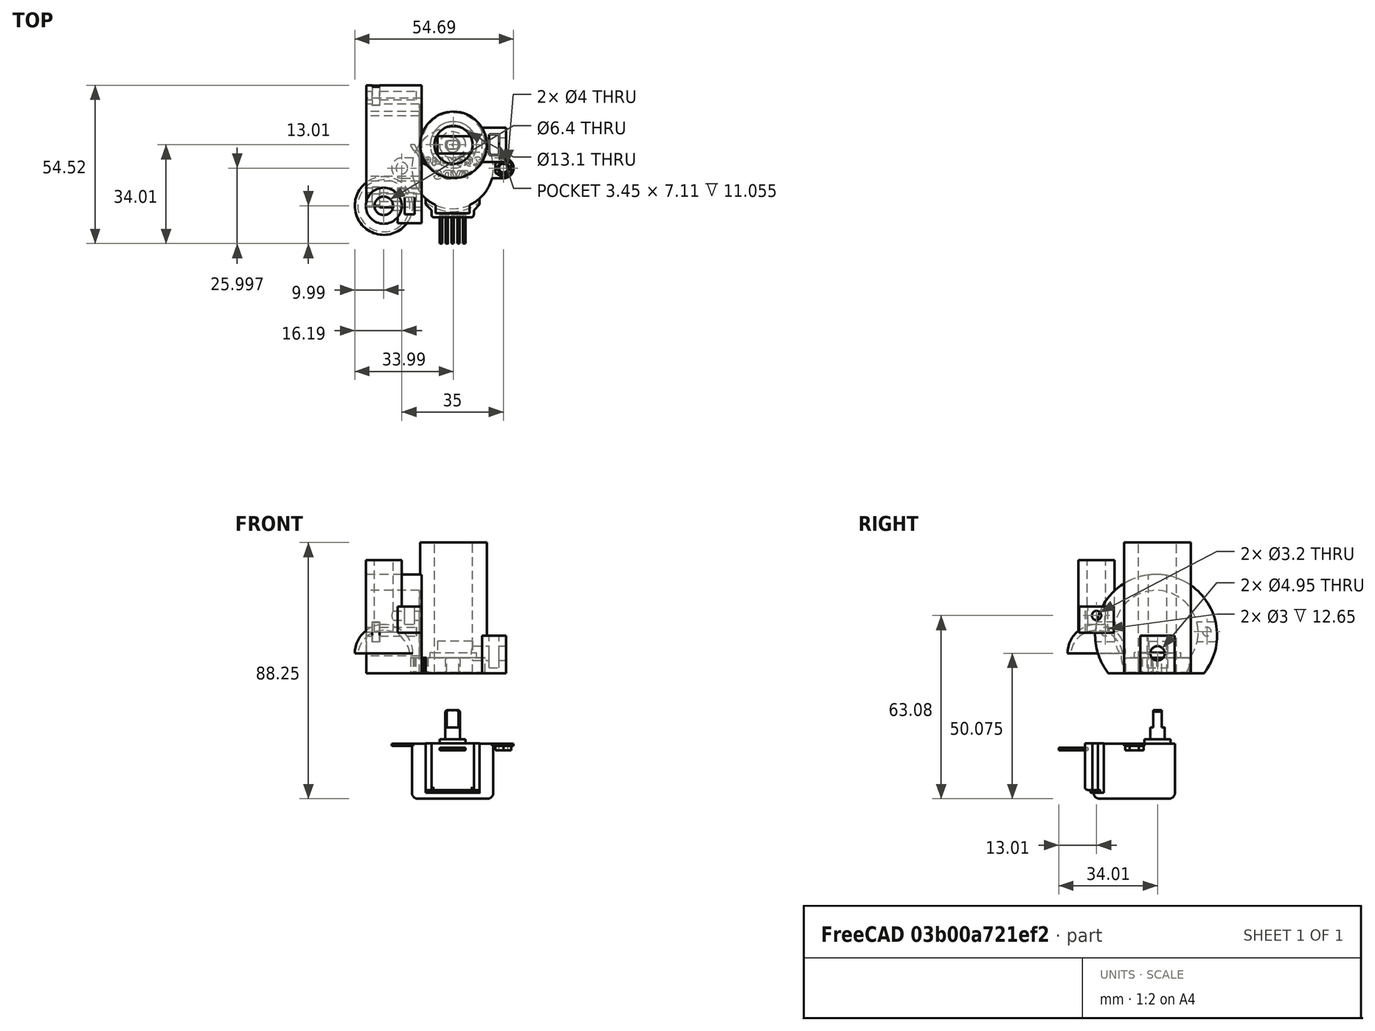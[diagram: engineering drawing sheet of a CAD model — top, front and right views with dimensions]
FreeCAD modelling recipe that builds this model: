
FCSTD DOCUMENT  (FreeCAD 0.19R24366 (Git))
Label: motor_fit
License: All rights reserved
LicenseURL: http://en.wikipedia.org/wiki/All_rights_reserved
objects: Part::Box×11, Part::Cylinder×10, Part::Cut×8, Part::Feature×5, Part::Fuse×4, Part::MultiFuse×4, Sketcher::SketchObject×3, Mesh::Feature×2, Part::Extrusion×2, Part::Sphere×2, Part::Compound×2
note: 51 computed .brp shape members not serialized (recipe doc carries the construction recipe); baked Part::Feature solids carry a one-line shape summary decoded from their .brp

FEATURE [Part::Cylinder] cylinder
  Angle = 360
  AttacherType = Attacher::AttachEngine3D
  Height = 45
  Radius = 11.45
FEATURE [Part::Box] cube
  AttacherType = Attacher::AttachEngine3D
  Height = 12.91
  Length = 8.25
  Placement = pos=(-4.125,-5.955,-6.455) rot=(0,0,1;0rad)
  Width = 11.91
FEATURE [Part::Box] cube001
  AttacherType = Attacher::AttachEngine3D
  Height = 11.11
  Length = 3.45
  Placement = pos=(-1.725,-3.555,-4.6) rot=(0,0,1;0rad)
  Width = 7.11
FEATURE [Part::Cut] difference
  Base = -> cube
  Placement = pos=(13.95,0,6.425) rot=(0,0,1;0rad)
  Tool = -> cube001
FEATURE [Part::Fuse] union
  Base = -> cylinder
  Tool = -> difference
FEATURE [Part::Cylinder] cylinder001
  Angle = 360
  AttacherType = Attacher::AttachEngine3D
  Height = 50
  Placement = pos=(0,0,-1) rot=(0,0,1;0rad)
  Radius = 6.55
FEATURE [Part::Cylinder] cylinder002
  Angle = 360
  AttacherType = Attacher::AttachEngine3D
  Height = 22.9
  Placement = pos=(0,0,6.825) rot=(0,1,0;1.5708rad)
  Radius = 2.475
FEATURE [Part::Fuse] union001
  Base = -> cylinder001
  Tool = -> cylinder002
FEATURE [Part::Cut] difference001  label="poleFit"
  Base = -> union
  Tool = -> union001
FEATURE [Mesh::Feature] Base
  Placement = pos=(0,0,0) rot=(1,0,0;1.5708rad)
FEATURE [Mesh::Feature] Freewheel_0_8mm  label="Freewheel_0.8mm"
  Placement = pos=(-63.4529,-2.9298,-37.056) rot=(0,0,1;0rad)
FEATURE [Sketcher::SketchObject] Sketch
  FullyConstrained = true
  Placement = pos=(0,0,0) rot=(0.57735,0.57735,0.57735;2.0944rad)
  sketch-geometry (37):
    g0: LineSegment StartX=76.2334 StartY=-16.1683 StartZ=0 EndX=76.2157 EndY=-16.287 EndZ=0
    g1: LineSegment StartX=76.2157 StartY=-16.287 StartZ=0 EndX=76.2042 EndY=-16.4372 EndZ=0
    g2: LineSegment StartX=76.2042 StartY=-16.4372 StartZ=0 EndX=76.2156 EndY=-16.5892 EndZ=0
    g3: LineSegment StartX=76.2156 StartY=-16.5892 StartZ=0 EndX=76.2528 EndY=-16.7393 EndZ=0
    g4: LineSegment StartX=76.2528 StartY=-16.7393 StartZ=0 EndX=76.312 EndY=-16.8829 EndZ=0
    g5: LineSegment StartX=76.312 StartY=-16.8829 StartZ=0 EndX=76.389 EndY=-17.0118 EndZ=0
    g6: LineSegment StartX=76.389 StartY=-17.0118 StartZ=0 EndX=76.4857 EndY=-17.1291 EndZ=0
    g7: LineSegment StartX=76.4857 StartY=-17.1291 StartZ=0 EndX=76.5997 EndY=-17.2306 EndZ=0
    g8: LineSegment StartX=76.5997 StartY=-17.2306 StartZ=0 EndX=76.7284 EndY=-17.3138 EndZ=0
    g9: LineSegment StartX=76.7284 StartY=-17.3138 StartZ=0 EndX=82.1149 EndY=-20.2387 EndZ=0
    g10: LineSegment StartX=82.1149 StartY=-20.2387 StartZ=0 EndX=82.1149 EndY=-21.7329 EndZ=0
    g11: LineSegment StartX=82.1149 StartY=-21.7329 StartZ=0 EndX=81.7891 EndY=-21.7293 EndZ=0
    g12: LineSegment StartX=81.7891 StartY=-21.7293 StartZ=0 EndX=80.304 EndY=-20.8014 EndZ=0
    g13: LineSegment StartX=80.304 StartY=-20.8014 StartZ=0 EndX=80.2423 EndY=-20.7557 EndZ=0
    g14: LineSegment StartX=80.2423 StartY=-20.7557 StartZ=0 EndX=80.188 EndY=-20.7011 EndZ=0
    g15: LineSegment StartX=80.188 StartY=-20.7011 StartZ=0 EndX=80.1429 EndY=-20.6389 EndZ=0
    g16: LineSegment StartX=80.1429 StartY=-20.6389 StartZ=0 EndX=80.1078 EndY=-20.5705 EndZ=0
    g17: LineSegment StartX=80.1078 StartY=-20.5705 StartZ=0 EndX=80.0837 EndY=-20.4975 EndZ=0
    g18: LineSegment StartX=80.0837 StartY=-20.4975 StartZ=0 EndX=80.071 EndY=-20.4217 EndZ=0
    g19: LineSegment StartX=80.071 StartY=-20.4217 StartZ=0 EndX=80.059 EndY=-20.2869 EndZ=0
    g20: LineSegment StartX=80.059 StartY=-20.2869 StartZ=0 EndX=80.0452 EndY=-20.2062 EndZ=0
    g21: LineSegment StartX=80.0452 StartY=-20.2062 StartZ=0 EndX=80.0182 EndY=-20.1286 EndZ=0
    g22: LineSegment StartX=80.0182 StartY=-20.1286 StartZ=0 EndX=79.9789 EndY=-20.0566 EndZ=0
    g23: LineSegment StartX=79.9789 StartY=-20.0566 StartZ=0 EndX=79.9285 EndY=-19.992 EndZ=0
    g24: LineSegment StartX=79.9285 StartY=-19.992 StartZ=0 EndX=79.8682 EndY=-19.9366 EndZ=0
    g25: LineSegment StartX=79.8682 StartY=-19.9366 StartZ=0 EndX=79.7996 EndY=-19.8917 EndZ=0
    g26: LineSegment StartX=79.7996 StartY=-19.8917 StartZ=0 EndX=76.3456 EndY=-18.0159 EndZ=0
    g27: LineSegment StartX=76.3456 StartY=-18.0159 StartZ=0 EndX=76.1153 EndY=-17.8672 EndZ=0
    g28: LineSegment StartX=76.1153 StartY=-17.8672 StartZ=0 EndX=75.9105 EndY=-17.6845 EndZ=0
    g29: LineSegment StartX=75.9105 StartY=-17.6845 StartZ=0 EndX=75.7345 EndY=-17.4732 EndZ=0
    g30: LineSegment StartX=75.7345 StartY=-17.4732 StartZ=0 EndX=75.5946 EndY=-17.2371 EndZ=0
    g31: LineSegment StartX=75.5946 StartY=-17.2371 StartZ=0 EndX=75.4903 EndY=-16.9821 EndZ=0
    g32: LineSegment StartX=75.4903 StartY=-16.9821 StartZ=0 EndX=75.4278 EndY=-16.7148 EndZ=0
    g33: LineSegment StartX=75.4278 StartY=-16.7148 StartZ=0 EndX=75.405 EndY=-16.4411 EndZ=0
    g34: LineSegment StartX=75.405 StartY=-16.4411 StartZ=0 EndX=75.4252 EndY=-16.1672 EndZ=0
    g35: LineSegment StartX=75.4252 StartY=-16.1672 StartZ=0 EndX=75.5014 EndY=-15.659 EndZ=0
    g36: ArcOfCircle CenterX=82.1156 CenterY=-6.93239 CenterZ=0 NormalX=0 NormalY=0 NormalZ=1 AngleXU=0 Radius=10.95 StartAngle=4.14528 EndAngle=10.347
  constraints (68):
    c: Coincident(g0,g1)
    c: Coincident(g1,g2)
    c: Coincident(g2,g3)
    c: Coincident(g3,g4)
    c: Coincident(g4,g5)
    c: Coincident(g5,g6)
    c: Coincident(g6,g7)
    c: Coincident(g7,g8)
    c: Coincident(g8,g9)
    c: Coincident(g9,g10)
    c: Vertical(g10)
    c: Coincident(g10,g11)
    c: Coincident(g11,g12)
    c: Coincident(g12,g13)
    c: Coincident(g13,g14)
    c: Coincident(g14,g15)
    c: Coincident(g15,g16)
    c: Coincident(g16,g17)
    c: Coincident(g17,g18)
    c: Coincident(g18,g19)
    c: Coincident(g19,g20)
    c: Coincident(g20,g21)
    c: Coincident(g21,g22)
    c: Coincident(g22,g23)
    c: Coincident(g23,g24)
    c: Coincident(g24,g25)
    c: Coincident(g25,g26)
    c: Coincident(g26,g27)
    c: Coincident(g27,g28)
    c: Coincident(g28,g29)
    c: Coincident(g29,g30)
    c: Coincident(g30,g31)
    c: Coincident(g31,g32)
    c: Coincident(g32,g33)
    c: Coincident(g33,g34)
    c: Coincident(g34,g35)
    c: Coincident(g36,g35)
    c: Coincident(g36,g0)
    c: Radius(g36) = 10.95
    c: Block(g35)
    c: Block(g1)
    c: Block(g0)
    c: Block(g2)
    c: Block(g3)
    c: Block(g4)
    c: Block(g5)
    c: Block(g6)
    c: Block(g34)
    c: Block(g33)
    c: Block(g32)
    c: Block(g31)
    c: Block(g30)
    c: Block(g29)
    c: Block(g28)
    c: Block(g27)
    c: Block(g7)
    c: Block(g8)
    c: Block(g9)
    c: Block(g26)
    c: Block(g11)
    c: Block(g12)
    c: Block(g14)
    c: Block(g17)
    c: Block(g20)
    c: Block(g22)
    c: Block(g24)
    c: Block(g19)
    c: Block(g16)
FEATURE [Part::Extrusion] Extrude
  Base = -> Sketch
  Dir = (1,0,0)
  DirMode = 2
  FaceMakerClass = Part::FaceMakerBullseye
  LengthFwd = 5
  LengthRev = 0
  Placement = pos=(6.88649,-82.0619,0.254467) rot=(0,1,0;1.5708rad)
  Solid = true
  Symmetric = false
FEATURE [Part::Cylinder] Cylinder006
  Angle = 360
  AttacherType = Attacher::AttachEngine3D
  Height = 6
  Radius = 8
FEATURE [Part::Box] Box003  label="Cube003"
  AttacherType = Attacher::AttachEngine3D
  Height = 25
  Length = 17
  Placement = pos=(-8.5,3,2) rot=(0,0,1;0rad)
  Width = 16
FEATURE [Part::Box] Box004  label="Cube004"
  AttacherType = Attacher::AttachEngine3D
  Height = 25
  Length = 17
  Placement = pos=(-8.5,-19,2) rot=(0,0,1;0rad)
  Width = 16
FEATURE [Part::Box] Box005  label="Cube005"
  AttacherType = Attacher::AttachEngine3D
  Height = 25
  Length = 17
  Placement = pos=(6.5,-3,2.1) rot=(0,0,1;0rad)
  Width = 16
FEATURE [Part::Box] Box006  label="Cube006"
  AttacherType = Attacher::AttachEngine3D
  Height = 25
  Length = 17
  Placement = pos=(-22.5,-12,2.1) rot=(0,0,1;0rad)
  Width = 16
FEATURE [Part::MultiFuse] Fusion001
  Shapes = -> [Box003,Box004,Box005,Box006]
FEATURE [Part::Cut] Cut004
  Base = -> Cylinder006
  Tool = -> Fusion001
FEATURE [Part::Box] cube002
  AttacherType = Attacher::AttachEngine3D
  Height = 8.91
  Length = 8.25
  Placement = pos=(-4.125,-5.955,-6.455) rot=(0,0,1;0rad)
  Width = 11.91
FEATURE [Part::Cylinder] cylinder003
  Angle = 360
  AttacherType = Attacher::AttachEngine3D
  Height = 50
  Placement = pos=(0,0,-1) rot=(0,0,1;0rad)
  Radius = 3.2
FEATURE [Part::Cylinder] cylinder004
  Angle = 360
  AttacherType = Attacher::AttachEngine3D
  Height = 25
  Radius = 6.2
FEATURE [Part::Box] cube003
  AttacherType = Attacher::AttachEngine3D
  Height = 11.11
  Length = 3.45
  Placement = pos=(-1.725,-2.9,-3.6) rot=(0,0,1;0rad)
  Width = 5.8
FEATURE [Part::Cylinder] cylinder005
  Angle = 360
  AttacherType = Attacher::AttachEngine3D
  Height = 22.9
  Placement = pos=(0,0,5.83) rot=(0,1,0;1.5708rad)
  Radius = 1.6
FEATURE [Part::Cut] difference002
  Base = -> cube002
  Placement = pos=(8.95,0,6.425) rot=(0,0,1;0rad)
  Tool = -> cube003
FEATURE [Part::Fuse] union002
  Base = -> cylinder003
  Tool = -> cylinder005
FEATURE [Part::Fuse] union003
  Base = -> cylinder004
  Tool = -> difference002
FEATURE [Part::Cut] difference003  label="wheel_fit_holder"
  Base = -> union003
  Tool = -> union002
FEATURE [Part::Sphere] Sphere
  Angle1 = -90
  Angle2 = 0
  Angle3 = 360
  AttacherType = Attacher::AttachEngine3D
  Placement = pos=(16.5428,-16.9323,-1e-16) rot=(0,0,1;0rad)
  Radius = 10
FEATURE [Part::Sphere] Sphere001
  Angle1 = -90
  Angle2 = 0
  Angle3 = 360
  AttacherType = Attacher::AttachEngine3D
  Placement = pos=(16.5428,-16.9323,1) rot=(0,0,1;0rad)
  Radius = 9
FEATURE [Part::Cut] Cut006
  Base = -> Sphere
  Placement = pos=(-0.04745,0.430952,1) rot=(0,0,1;0rad)
  Tool = -> Sphere001
FEATURE [Sketcher::SketchObject] Sketch002
  FullyConstrained = true
  MapMode = 3
  Placement = pos=(0,0,0) rot=(1,0,0;3.14159rad)
  Support = -> [Base]
  sketch-geometry (1):
    g0: Circle CenterX=16.4953 CenterY=16.5013 CenterZ=0 NormalX=0 NormalY=0 NormalZ=1 AngleXU=0 Radius=8
  constraints (2):
    c: Radius(g0) = 8
    c: Block(g0)
FEATURE [Part::Feature] Base002
  shape: bbox 32.96 x 33 x 8 mm, 664 faces, 0 solids (baked)
FEATURE [Part::Compound] Compound001
  Links = -> [Cut006,Base002]
  Placement = pos=(-16.49,-16.5,-6.25) rot=(1,0,0;3.14159rad)
FEATURE [Part::Compound] Compound002  label="wheel_assembly"
  Links = -> [difference003,Compound001]
  Placement = pos=(-24,-21,14) rot=(0,0,1;0rad)
FEATURE [Part::Feature] Part__Feature  label="stepper_rendering"
  Placement = pos=(-0.300362,-8.01257,-24.25) rot=(-1,0,0;1.5708rad)
  shape: bbox 42 x 41.15 x 30.5 mm, 152 faces (baked)
FEATURE [Sketcher::SketchObject] Sketch003
  FullyConstrained = true
  MapMode = 5
  Placement = pos=(-0.300362,-8.01257,-12.75) rot=(0,0,1;0rad)
  Support = -> [Part__Feature]
  sketch-geometry (4):
    g0: LineSegment StartX=-2.08854 StartY=9.51445 StartZ=0 EndX=2.11146 EndY=9.51445 EndZ=0
    g1: LineSegment StartX=-2.09836 StartY=6.52273 StartZ=0 EndX=2.10164 EndY=6.52273 EndZ=0
    g2: ArcOfCircle CenterX=-0.003655 CenterY=8.01173 CenterZ=0 NormalX=0 NormalY=0 NormalZ=1 AngleXU=0 Radius=2.57 StartAngle=2.51706 EndAngle=3.75956
    g3: ArcOfCircle CenterX=0.004473 CenterY=8.02549 CenterZ=0 NormalX=0 NormalY=0 NormalZ=1 AngleXU=0 Radius=2.58 StartAngle=5.66143 EndAngle=6.89838
  constraints (14):
    c: Horizontal(g0)
    c: Horizontal(g1)
    c: Coincident(g2,g0)
    c: Coincident(g2,g1)
    c: Coincident(g3,g0)
    c: Coincident(g3,g1)
    c: DistanceX(g0,g0) = 4.2
    c: DistanceX(g1,g1) = 4.2
    c: DistanceX(g2) = -0.003655
    c: DistanceY(g2) = 8.01173
    c: DistanceX(g3) = 0.004473
    c: DistanceY(g3) = 8.02549
    c: Radius(g3) = 2.58
    c: Radius(g2) = 2.57
FEATURE [Part::Extrusion] Extrude001  label="stepper_axis"
  Base = -> Sketch003
  Dir = (0,-2e-16,1)
  DirMode = 2
  FaceMakerClass = Part::FaceMakerBullseye
  LengthFwd = 10
  LengthRev = 0
  Placement = pos=(0,0,3) rot=(0,0,1;0rad)
  Solid = true
  Symmetric = false
FEATURE [Part::MultiFuse] Fusion002
  Shapes = -> [Extrude,Cut004]
FEATURE [Part::Cut] Cut007  label="clutch_fit"
  Base = -> Fusion002
  Placement = pos=(0,0,5) rot=(0,0,1;0rad)
  Tool = -> Extrude001
FEATURE [Part::Cylinder] Cylinder
  Angle = 360
  AttacherType = Attacher::AttachEngine3D
  Height = 19
  Placement = pos=(-0.3,-9.31302,-37) rot=(0,0,1;0rad)
  Radius = 21
FEATURE [Part::Cylinder] Cylinder007
  Angle = 360
  AttacherType = Attacher::AttachEngine3D
  Height = 20
  Placement = pos=(-0.300362,-8.31,-36.25) rot=(0,0,1;0rad)
  Radius = 14.5
FEATURE [Part::Cylinder] Cylinder008
  Angle = 360
  AttacherType = Attacher::AttachEngine3D
  Height = 20
  Placement = pos=(-0.300362,-16.31,-36.25) rot=(0,0,1;0rad)
  Radius = 12
FEATURE [Part::Feature] BOLTS_part  label="Hex socket countersunk head screw M3 20.0"
  Placement = pos=(17.1996,-8.01257,-15.25) rot=(1,0,0;3.14159rad)
  shape: bbox 6 x 6 x 20 mm, 12 faces (baked)
FEATURE [Part::Feature] BOLTS_part001  label="Metric hexagon nut M3"
  Placement = pos=(17.1996,-8.01257,-26.65) rot=(0,0,1;0rad)
  shape: bbox 5.5 x 6.351 x 2.4 mm, 9 faces (baked)
FEATURE [Part::Box] Box  label="Cube"
  AttacherType = Attacher::AttachEngine3D
  Height = 2.6
  Length = 7
  Placement = pos=(13.8,-11.5126,-22.6) rot=(0,0,1;0rad)
  Width = 6.8
FEATURE [Part::Box] Box007  label="Cube007"
  AttacherType = Attacher::AttachEngine3D
  Height = 2.6
  Length = 7
  Placement = pos=(-21.3004,-11.5126,-22.6) rot=(0,0,1;0rad)
  Width = 6.8
FEATURE [Part::Feature] BOLTS_part002  label="Hex socket countersunk head screw M3 20.001"
  Placement = pos=(-17.8004,-8.01257,-15.25) rot=(1,0,0;3.14159rad)
  shape: bbox 6 x 6 x 20 mm, 12 faces (baked)
FEATURE [Part::Box] Box009  label="Cube009"
  AttacherType = Attacher::AttachEngine3D
  Height = 20
  Length = 46
  Placement = pos=(-23.3,-46.31,-37) rot=(0,0,1;0rad)
  Width = 24
FEATURE [Part::MultiFuse] Fusion
  Shapes = -> [Box009,BOLTS_part002,Box007,Box,BOLTS_part,Cylinder008,Cylinder007]
FEATURE [Part::Cut] Cut  label="motor_fit"
  Base = -> Cylinder
  Placement = pos=(-48,-0.79,22.31) rot=(0.57735,-0.57735,-0.57735;2.0944rad)
  Tool = -> Fusion
FEATURE [Part::MultiFuse] Fusion003  label="final_part"
  Shapes = -> [difference001,Cut]
